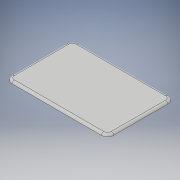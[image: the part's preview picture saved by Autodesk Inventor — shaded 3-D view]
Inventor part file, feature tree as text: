
AUTODESK INVENTOR PART (.ipt)
format: ipt  version: 2019 (Build 230136000, 136)  size: 306,688 bytes
history: native  units: in
note: dims shown in document units (in); Inventor stores cm internally (conversion verified against a paired STEP export)
features: sketch x3, extrude x2, fillet x2
ambient origin geometry x8: Origin, YZ Plane, XZ Plane, XY Plane, X Axis, Y Axis, Z Axis, Center Point
bodies: Solid1 (feature_tree)
feature tree (7):
  sketch  "Sketch1"  dims[d0=5.0in d1=3.189in]
  extrude  "Extrusion1"  Depth=3.189in
  extrude  "Extrusion2"  Depth=0.0787in TaperAngle=0.0deg
  fillet  "Fillet1"  Radius=0.2756in
  fillet  "Fillet2"  Radius=0.1181in
  sketch  "Sketch2"  dims[d2=0.1575in d3=0.0787in d4=0.0in d5=0.2756in d6=0.1181in]
  sketch  "Sketch3"  dims[d7=5.2362in d8=3.4252in d9=0.315in d10=0.315in d11=0.1181in d12=0.0in d13=0.1181in d14=0.0394in]
